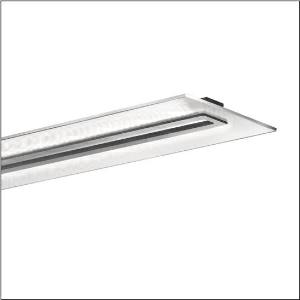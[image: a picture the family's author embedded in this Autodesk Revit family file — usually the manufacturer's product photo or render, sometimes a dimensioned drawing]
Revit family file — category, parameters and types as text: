
# Revit family: vega_11_5mn238dle0s3
name_source: partatom
category: Lighting Fixtures
units: mm (PartAtom-declared; Revit-internal decimal feet)

## family parameters
Cut with Voids When Loaded = No
Host = Face
Light Source = No
Part Type = Normal
Room Calculation Point = No
Round Connector Dimension = Use Diameter
Shared = No

## types (1)
- --- (1 x LED 3000K / CRI = 80 (unbekannt), 7300 lm, 3000K)
    Apparent Load = 62 VA
    CIE Flux Codes = 61 86 97 62 100
    Color Rendering = 80
    Color Temperature = 3000K
    Default Elevation = 1800 mm
    Description = Vega 11, office luminaire, primary light control with prismatic reflector, of PMMA, transparent prismatic structure, CAT 2 (L<= 1500cd/m²), light emission: direct/indirect distribution, primary light characteristic: symmetric, installation type: suspended mounting, surface-mounted, LED, rated luminous flux: 7.300lm, luminous efficacy: 118lm/W, light colour: 830, colour temperature: 3000K, control gear: DALI, with terminal, 3+2-pole, max. 2.5mm², mains connection: 230V, AC, 50Hz, connection cable inclusive, cable length: 1,5m, rated input power: 62W, luminaire housing, rectangular, rounded, of aluminium section, anodised, metallic grey (RAL 9006), length: 1.250mm, width: 350mm, height: 43mm, luminaire housing, lower part, of aluminium section, anodised, metallic grey (RAL 9006), of PC, grey, protection rating (complete): IP20, insulation class (complete): insulation class I (protective earthing), certification: CE, permissible operating ambient temperature: 0..+35°C, standard: EN 50419, packaging unit: 1 piece
    Height = 40 mm  [stored 0.131234 ft]
    Lamp = 1 x LED 3000K / CRI >= 80 (unbekannt)
    Lamp Light Flux = 7300 lm
    Lamp count = 1
    Length = 1250 mm
    Luminous efficacy = 118 lm/W
    Manufacturer = Siteco
    ModVariant = No
    Model = 5MN238DLE0S3
    Mounting Place = Ceiling
    Mounting Type = Pendant
    Number of Poles = 1
    OnlyDefault = Yes
    Power Factor = 1
    Product Name = Vega 11
    Product group = office luminaire | ceiling pendant
    ProductGroupID = 903
    Protection Class = Protection class I
    Protection Degree = IP 20
    RLX_Detail_Level = 1
    RLX_Emergency_Light_Flux = 0 lm
    RLX_Emergency_Type = 0
    RLX_Emergency_Type_DB = No
    RlxData = <blob elided: 62797 chars, md5=4f7781cf>
    Socket = socket
    Standby Power = 0 W
    System Light Flux = 7300 lm
    System Power = 62 W
    Type Comments = factory setting: luminous flux: 100 % | dim-lin: 254 | 460 mA
    Type Image = l_1004807.jpg
    URL = http://relux.com
    VarID = @adj_198539
    Voltage = 0 V
    Weight = 0.00 kg
    Width = 350 mm

note: [stored X ft] marks values corroborated as IEEE doubles in the binary element streams (Revit-internal decimal feet)

## geometry (parser evidence)
native form markers: Blend x4, Sweep x13
no freeform markers — native parametric forms only
